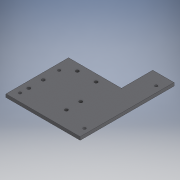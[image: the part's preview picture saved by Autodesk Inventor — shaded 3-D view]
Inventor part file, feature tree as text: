
AUTODESK INVENTOR PART (.ipt)
format: ipt  version: 2018 (Build 220112000, 112)  size: 144,896 bytes
history: native  units: mm
features: thread x4, extrude x1, sketch x1
ambient origin geometry x8: Origin, YZ Plane, XZ Plane, XY Plane, X Axis, Y Axis, Z Axis, Center Point
bodies: Solid1 (feature_tree)
feature tree (6):
  extrude  "Extrusion1"  Depth=10.0mm
  thread  "Thread1"  [1 undecoded]
  thread  "Thread2"  [1 undecoded]
  thread  "Thread3"  [1 undecoded]
  thread  "Thread4"  [1 undecoded]
  sketch  "Sketch1"  dims[d82=10.0mm d83=60.0mm d86=110.0mm d87=90.0mm d88=92.0mm d90=300.0mm d91=200.0mm d92=35.0mm d93=68.0mm d94=100.0mm d95=237.0mm d96=79.0mm d98=60.0mm d100=46.0mm d101=8.5mm d102=140.0mm d103=80.0mm d104=3.0mm d105=152.0mm d106=61.0mm d107=85.0mm d108=40.0mm d109=10.0mm d110=0.0mm d119=10.0mm d120=0.0mm d121=10.0mm d122=0.0mm d123=10.0mm d124=0.0mm d125=10.0mm d126=0.0mm d136=12.0mm d139=20.0mm]
note: 4 required parameter values undecoded (feature->parameter linkage not recoverable at this tier; creation-order binding heuristic only, values carry confidence <= 0.55)
